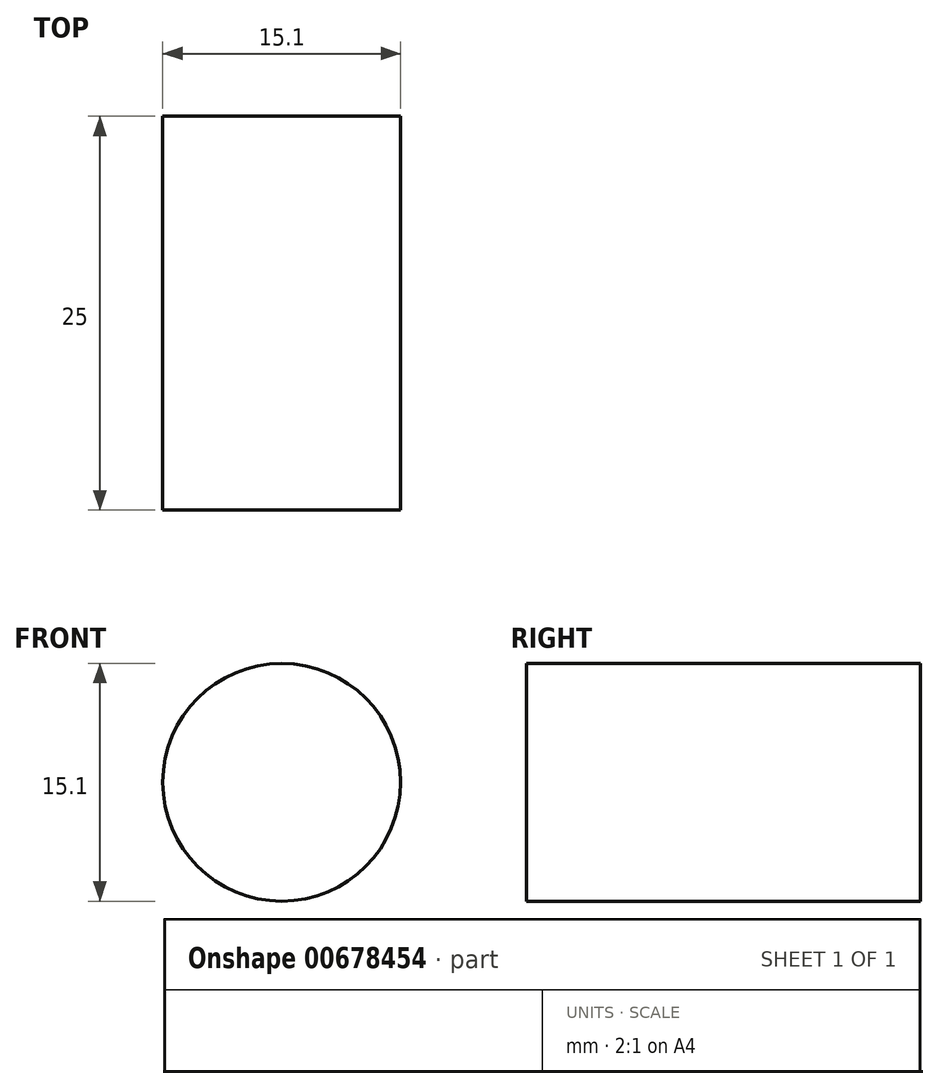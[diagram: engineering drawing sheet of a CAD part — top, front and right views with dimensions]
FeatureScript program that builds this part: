
annotation { "Feature Type Name" : "Feature", "Feature Type Description" : "" }
export const myFeature = defineFeature(function(context is Context, id is Id, definition is map)
    precondition{}
    {
        {
            var Q0;
            Q0=qCreatedBy(makeId("Front.planeOp"),FACE);
            var sketch = newSketch(context, id + "F0", { "sketchPlane" : qUnion([Q0])});
            skCircle(sketch, "E0", {"center": v(0, 0) * mm, "radius": 7.55 * mm});
            skSolve(sketch);
        }
        {
            var Q0;
            Q0 = qSketchRegion(id + "F0", true);
            extrude(context, id + "F1", {"entities" : qUnion([Q0]), "depth" : 25 * mm, "offsetDistance" : 25 * mm});
        }
    });
